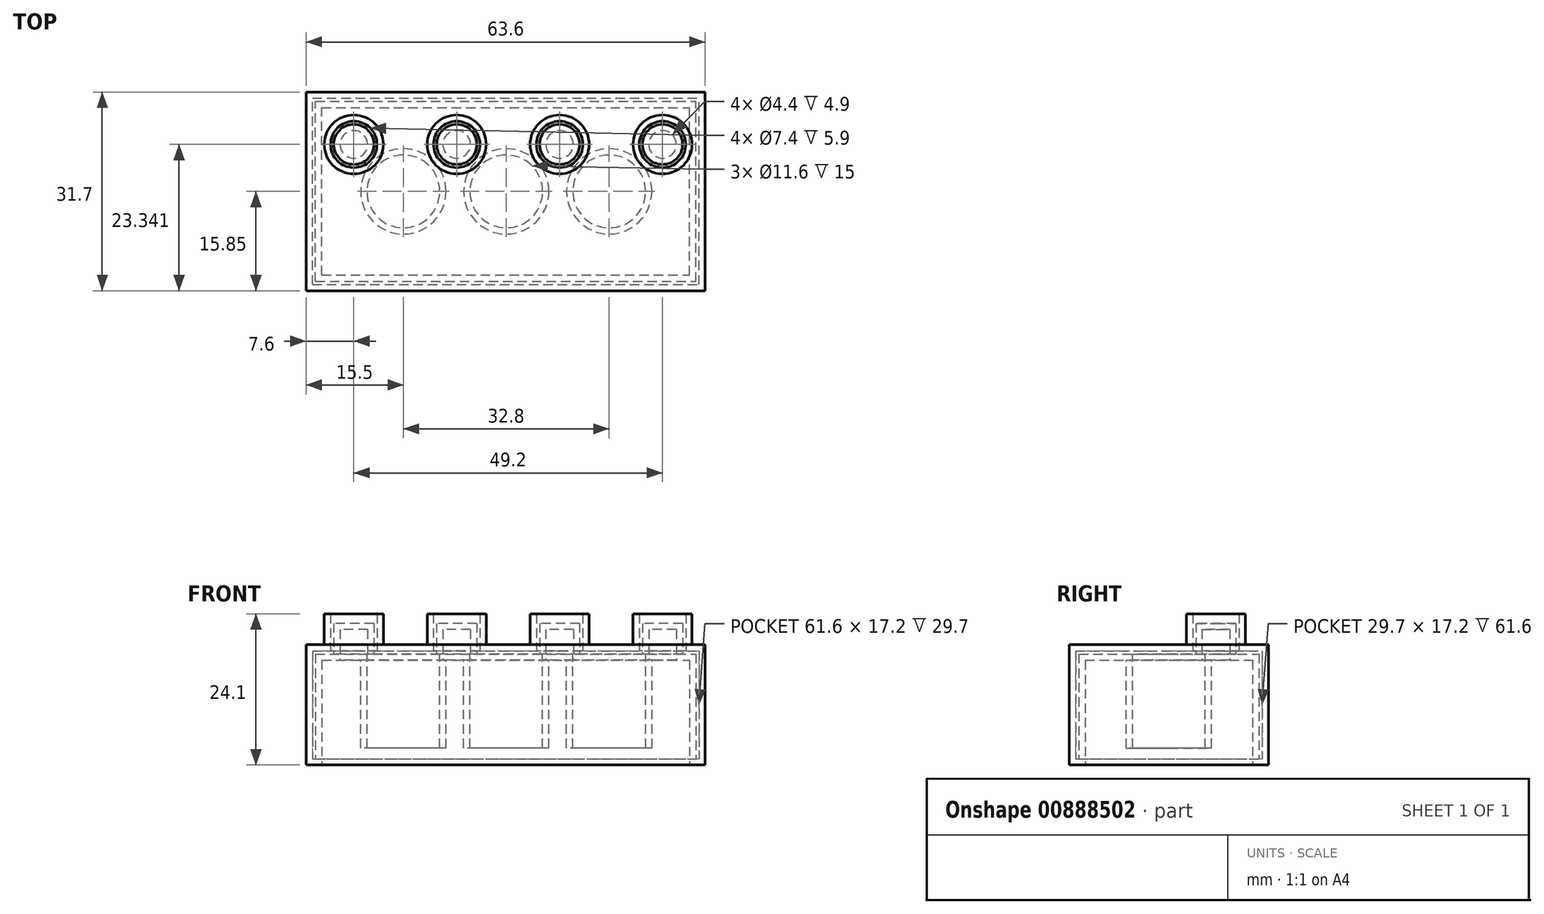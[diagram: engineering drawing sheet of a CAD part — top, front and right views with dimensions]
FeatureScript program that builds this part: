
annotation { "Feature Type Name" : "Feature", "Feature Type Description" : "" }
export const myFeature = defineFeature(function(context is Context, id is Id, definition is map)
    precondition{}
    {
        {
            var Q0;
            Q0=qCreatedBy(makeId("Front.planeOp"),FACE);
            var sketch = newSketch(context, id + "F0", { "sketchPlane" : qUnion([Q0])});
            skLineSegment(sketch, "E0.bottom", {"start": v(-31.8, 0) * mm, "end": v(31.8, 0) * mm});
            skLineSegment(sketch, "E0.top", {"start": v(-31.8, -19.2) * mm, "end": v(31.8, -19.2) * mm});
            skLineSegment(sketch, "E0.left", {"start": v(-31.8, 0) * mm, "end": v(-31.8, -19.2) * mm});
            skLineSegment(sketch, "E0.right", {"start": v(31.8, 0) * mm, "end": v(31.8, -19.2) * mm});
            skSolve(sketch);
        }
        {
            var Q0;
            Q0 = qSketchRegion(id + "F0", true);
            extrude(context, id + "F1", {"entities" : qUnion([Q0]), "endBound" : BoundingType.SYMMETRIC, "depth" : 31.7 * mm, "offsetDistance" : 25 * mm});
        }
        {
            var Q0;
            Q0=qCreatedBy(makeId("Top.planeOp"),FACE);
            var sketch = newSketch(context, id + "F2", { "sketchPlane" : qUnion([Q0])});
            skCircle(sketch, "E1", {"center": v(-24.2, 7.5) * mm, "radius": 4.7 * mm});
            skCircle(sketch, "E2.1.0.0", {"center": v(-7.8, 7.5) * mm, "radius": 4.7 * mm});
            skCircle(sketch, "E2.2.0.0", {"center": v(8.6, 7.5) * mm, "radius": 4.7 * mm});
            skCircle(sketch, "E2.3.0.0", {"center": v(25, 7.5) * mm, "radius": 4.7 * mm});
            skLineSegment(sketch, "E2.direction1", {"start": v(-24.2, 7.5) * mm, "end": v(-7.8, 7.5) * mm, "construction": true});
            skCircle(sketch, "E3.MirrorC", {"center": v(-24.2, -7.5) * mm, "radius": 4.7 * mm});
            skCircle(sketch, "E4.MirrorC", {"center": v(-7.8, -7.5) * mm, "radius": 4.7 * mm});
            skCircle(sketch, "E5.MirrorC", {"center": v(8.6, -7.5) * mm, "radius": 4.7 * mm});
            skCircle(sketch, "E6.MirrorC", {"center": v(25, -7.5) * mm, "radius": 4.7 * mm});
            skSolve(sketch);
        }
        {
            var Q0;
            Q0=makeQuery(id+"F2.imprint","IMPRINT",FACE,{"disambiguationData":[TD([[makeQuery(id+"F2.imprint","IMPRINT",EDGE,{"derivedFrom":sQuery(id+"F2.wireOp",EDGE,"E1")}),1.0]])]});
            var Q1;
            Q1=makeQuery(id+"F2.imprint","IMPRINT",FACE,{"disambiguationData":[TD([[makeQuery(id+"F2.imprint","IMPRINT",EDGE,{"derivedFrom":sQuery(id+"F2.wireOp",EDGE,"E2.1.0.0")}),1.0]])]});
            var Q2;
            Q2=makeQuery(id+"F2.imprint","IMPRINT",FACE,{"disambiguationData":[TD([[makeQuery(id+"F2.imprint","IMPRINT",EDGE,{"derivedFrom":sQuery(id+"F2.wireOp",EDGE,"E2.2.0.0")}),1.0]])]});
            var Q3;
            Q3=makeQuery(id+"F2.imprint","IMPRINT",FACE,{"disambiguationData":[TD([[makeQuery(id+"F2.imprint","IMPRINT",EDGE,{"derivedFrom":sQuery(id+"F2.wireOp",EDGE,"E2.3.0.0")}),1.0]])]});
            var Q4;
            Q4=makeQuery(id+"F2.imprint","IMPRINT",FACE,{"disambiguationData":[TD([[makeQuery(id+"F2.imprint","IMPRINT",EDGE,{"derivedFrom":sQuery(id+"F2.wireOp",EDGE,"E6.MirrorC")}),-1.0]])]});
            var Q5;
            Q5=makeQuery(id+"F2.imprint","IMPRINT",FACE,{"disambiguationData":[TD([[makeQuery(id+"F2.imprint","IMPRINT",EDGE,{"derivedFrom":sQuery(id+"F2.wireOp",EDGE,"E5.MirrorC")}),-1.0]])]});
            var Q6;
            Q6=makeQuery(id+"F2.imprint","IMPRINT",FACE,{"disambiguationData":[TD([[makeQuery(id+"F2.imprint","IMPRINT",EDGE,{"derivedFrom":sQuery(id+"F2.wireOp",EDGE,"E4.MirrorC")}),-1.0]])]});
            var Q7;
            Q7=makeQuery(id+"F2.imprint","IMPRINT",FACE,{"disambiguationData":[TD([[makeQuery(id+"F2.imprint","IMPRINT",EDGE,{"derivedFrom":sQuery(id+"F2.wireOp",EDGE,"E3.MirrorC")}),-1.0]])]});
            extrude(context, id + "F3", {"entities" : qUnion([Q0, Q1, Q2, Q3, Q4, Q5, Q6, Q7]), "operationType" : NewBodyOperationType.ADD, "depth" : 4.9 * mm, "offsetDistance" : 25 * mm});
        }
        {
            var Q0;
            Q0=makeQuery(id+"F1.opExtrude","SWEPT_FACE",FACE,{"disambiguationData":[OSD([sQuery(id+"F0.wireOp",EDGE,"E0.top")])]});
            shell(context, id + "F4", {"entities" : qUnion([Q0]), "thickness" : 2.5 * mm});
        }
        {
            var Q0;
            Q0=qCreatedBy(makeId("Top.planeOp"),FACE);
            var sketch = newSketch(context, id + "F5", { "sketchPlane" : qUnion([Q0])});
            skCircle(sketch, "E7", {"center": v(16.5, 0) * mm, "radius": 6.8 * mm});
            skCircle(sketch, "E8.1.0.0", {"center": v(0.1, 0) * mm, "radius": 6.8 * mm});
            skCircle(sketch, "E8.2.0.0", {"center": v(-16.3, 0) * mm, "radius": 6.8 * mm});
            skLineSegment(sketch, "E9", {"start": v(-9.5, 0) * mm, "end": v(-6.7, 0) * mm});
            skLineSegment(sketch, "E10", {"start": v(6.9, 0) * mm, "end": v(9.7, 0) * mm});
            skLineSegment(sketch, "E11", {"start": v(0, 15.95) * mm, "end": v(0.1, 6.8) * mm});
            skLineSegment(sketch, "E12", {"start": v(0, -16.12) * mm, "end": v(0, -6.8) * mm});
            skSolve(sketch);
        }
        {
            var Q0;
            Q0=makeQuery(id+"F5.imprint","IMPRINT",FACE,{"disambiguationData":[TD([[makeQuery(id+"F5.imprint","IMPRINT",EDGE,{"derivedFrom":sQuery(id+"F5.wireOp",EDGE,"E8.2.0.0")}),1.0]])]});
            var Q1;
            {var subQ0=sQuery(id+"F5.wireOp",EDGE,"E8.1.0.0");var subQ1=makeQuery(id+"F5.imprint","IMPRINT",VERTEX,{"disambiguationData":[OD(1.0)],"derivedFrom":subQ0});Q1=makeQuery(id+"F5.imprint","IMPRINT",FACE,{"disambiguationData":[TD([[makeQuery(id+"F5.imprint","IMPRINT",EDGE,{"disambiguationData":[TD([[subQ1,-1.0]])],"derivedFrom":subQ0}),1.0]])]});}
            var Q2;
            Q2=makeQuery(id+"F5.imprint","IMPRINT",FACE,{"disambiguationData":[TD([[makeQuery(id+"F5.imprint","IMPRINT",EDGE,{"derivedFrom":sQuery(id+"F5.wireOp",EDGE,"E7")}),1.0]])]});
            extrude(context, id + "F6", {"entities" : qUnion([Q0, Q1, Q2]), "operationType" : NewBodyOperationType.ADD, "oppositeDirection" : true, "depth" : 16.5 * mm, "offsetDistance" : 25 * mm});
        }
        {
            var Q0;
            Q0=makeQuery(id+"F6.opExtrude","CAP_FACE",FACE,{"disambiguationData":[OSD([sQuery(id+"F5.wireOp",EDGE,"E7")])],"isStart":false});
            var Q1;
            Q1=makeQuery(id+"F6.opExtrude","CAP_FACE",FACE,{"disambiguationData":[OSD([sQuery(id+"F5.wireOp",EDGE,"E8.1.0.0")])],"isStart":false});
            var Q2;
            Q2=makeQuery(id+"F6.opExtrude","CAP_FACE",FACE,{"disambiguationData":[OSD([sQuery(id+"F5.wireOp",EDGE,"E8.2.0.0")])],"isStart":false});
            var Q3;
            Q3=makeQuery(id+"F3.opExtrude","CAP_FACE",FACE,{"disambiguationData":[OSD([sQuery(id+"F2.wireOp",EDGE,"E3.MirrorC")])],"isStart":false});
            var Q4;
            Q4=makeQuery(id+"F3.opExtrude","CAP_FACE",FACE,{"disambiguationData":[OSD([sQuery(id+"F2.wireOp",EDGE,"E1")])],"isStart":false});
            var Q5;
            Q5=makeQuery(id+"F3.opExtrude","CAP_FACE",FACE,{"disambiguationData":[OSD([sQuery(id+"F2.wireOp",EDGE,"E2.1.0.0")])],"isStart":false});
            var Q6;
            Q6=makeQuery(id+"F3.opExtrude","CAP_FACE",FACE,{"disambiguationData":[OSD([sQuery(id+"F2.wireOp",EDGE,"E4.MirrorC")])],"isStart":false});
            var Q7;
            Q7=makeQuery(id+"F3.opExtrude","CAP_FACE",FACE,{"disambiguationData":[OSD([sQuery(id+"F2.wireOp",EDGE,"E5.MirrorC")])],"isStart":false});
            var Q8;
            Q8=makeQuery(id+"F3.opExtrude","CAP_FACE",FACE,{"disambiguationData":[OSD([sQuery(id+"F2.wireOp",EDGE,"E2.2.0.0")])],"isStart":false});
            var Q9;
            Q9=makeQuery(id+"F3.opExtrude","CAP_FACE",FACE,{"disambiguationData":[OSD([sQuery(id+"F2.wireOp",EDGE,"E2.3.0.0")])],"isStart":false});
            var Q10;
            Q10=makeQuery(id+"F3.opExtrude","CAP_FACE",FACE,{"disambiguationData":[OSD([sQuery(id+"F2.wireOp",EDGE,"E6.MirrorC")])],"isStart":false});
            shell(context, id + "F7", {"entities" : qUnion([Q0, Q1, Q2, Q3, Q4, Q5, Q6, Q7, Q8, Q9, Q10]), "thickness" : 1 * mm});
        }
    });
